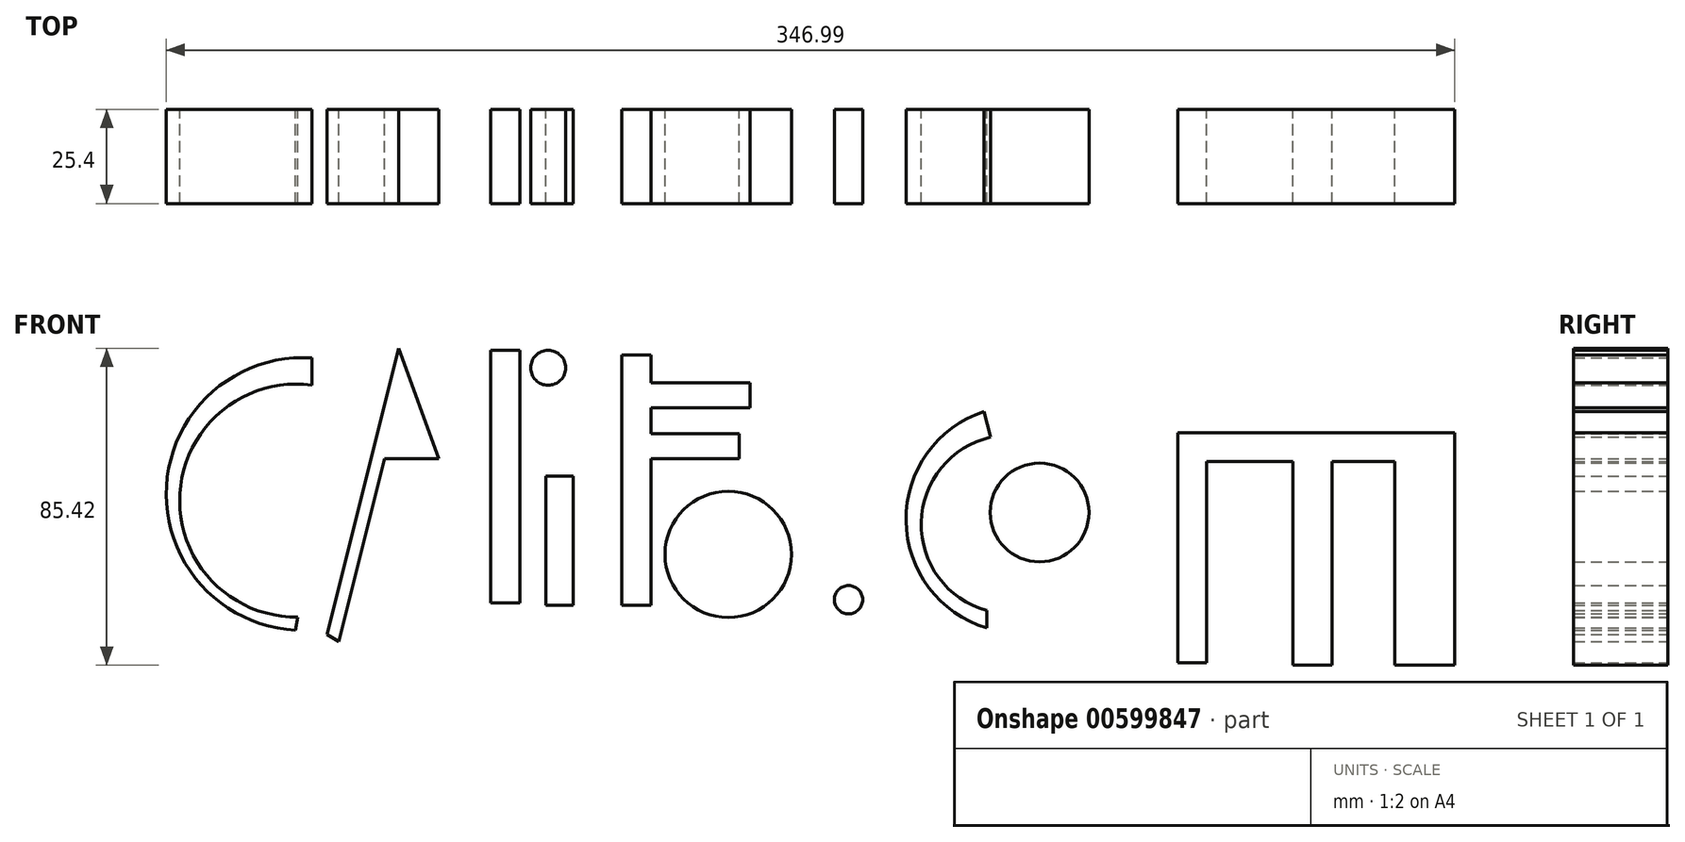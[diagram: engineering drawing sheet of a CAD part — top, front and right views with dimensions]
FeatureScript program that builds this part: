
annotation { "Feature Type Name" : "Feature", "Feature Type Description" : "" }
export const myFeature = defineFeature(function(context is Context, id is Id, definition is map)
    precondition{}
    {
        {
            var Q0;
            Q0=qCreatedBy(makeId("Front.planeOp"),FACE);
            var sketch = newSketch(context, id + "F0", { "sketchPlane" : qUnion([Q0])});
            skArc(sketch, "E0", {"start": v(-27.89, 41.61) * mm, "mid": v(-67, 7.17) * mm, "end": v(-32.27, -31.68) * mm});
            skLineSegment(sketch, "E1", {"start": v(-4.53, 44.24) * mm, "end": v(-23.8, -32.85) * mm});
            skLineSegment(sketch, "E2", {"start": v(-4.53, 44.24) * mm, "end": v(20.3, -24.38) * mm});
            skLineSegment(sketch, "E3", {"start": v(6.25, 14.44) * mm, "end": v(-11.97, 14.44) * mm});
            skLineSegment(sketch, "E4", {"start": v(28.12, 43.68) * mm, "end": v(28.12, -24.97) * mm});
            skLineSegment(sketch, "E5", {"start": v(35.19, 19.13) * mm, "end": v(35.19, -24.38) * mm});
            skCircle(sketch, "E6", {"center": v(35.77, 38.98) * mm, "radius": 4.7 * mm});
            skLineSegment(sketch, "E7", {"start": v(55.63, 42.49) * mm, "end": v(55.63, -22.63) * mm});
            skLineSegment(sketch, "E8", {"start": v(55.63, -22.63) * mm, "end": v(55.63, 34.9) * mm});
            skLineSegment(sketch, "E9", {"start": v(55.63, 34.9) * mm, "end": v(75.78, 34.9) * mm});
            skLineSegment(sketch, "E10", {"start": v(55.63, 21.17) * mm, "end": v(77.24, 21.17) * mm});
            skLineSegment(sketch, "E11.bottom", {"start": v(35.19, 9.78) * mm, "end": v(42.49, 9.78) * mm});
            skLineSegment(sketch, "E11.top", {"start": v(35.19, -24.97) * mm, "end": v(42.49, -24.97) * mm});
            skLineSegment(sketch, "E11.left", {"start": v(35.19, 9.78) * mm, "end": v(35.19, -24.97) * mm});
            skLineSegment(sketch, "E11.right", {"start": v(42.49, 9.78) * mm, "end": v(42.49, -24.97) * mm});
            skLineSegment(sketch, "E12.bottom", {"start": v(55.63, 34.9) * mm, "end": v(55.63, 34.9) * mm});
            skLineSegment(sketch, "E12.top", {"start": v(55.63, 42.49) * mm, "end": v(55.63, 42.49) * mm});
            skLineSegment(sketch, "E12.left", {"start": v(55.63, 34.9) * mm, "end": v(55.63, 42.49) * mm});
            skLineSegment(sketch, "E12.right", {"start": v(55.63, 34.9) * mm, "end": v(55.63, 42.49) * mm});
            skLineSegment(sketch, "E13.bottom", {"start": v(55.63, 42.49) * mm, "end": v(63.51, 42.49) * mm});
            skLineSegment(sketch, "E13.top", {"start": v(55.63, -24.97) * mm, "end": v(63.51, -24.97) * mm});
            skLineSegment(sketch, "E13.left", {"start": v(55.63, 42.49) * mm, "end": v(55.63, -24.97) * mm});
            skLineSegment(sketch, "E13.right", {"start": v(63.51, 42.49) * mm, "end": v(63.51, -24.97) * mm});
            skLineSegment(sketch, "E14.bottom", {"start": v(55.63, 34.9) * mm, "end": v(90.08, 34.9) * mm});
            skLineSegment(sketch, "E14.top", {"start": v(55.63, 28.18) * mm, "end": v(90.08, 28.18) * mm});
            skLineSegment(sketch, "E14.left", {"start": v(55.63, 34.9) * mm, "end": v(55.63, 28.18) * mm});
            skLineSegment(sketch, "E14.right", {"start": v(90.08, 34.9) * mm, "end": v(90.08, 28.18) * mm});
            skLineSegment(sketch, "E15.bottom", {"start": v(55.63, 14.44) * mm, "end": v(87.16, 14.44) * mm});
            skLineSegment(sketch, "E15.top", {"start": v(55.63, 21.17) * mm, "end": v(87.16, 21.17) * mm});
            skLineSegment(sketch, "E15.left", {"start": v(55.63, 14.44) * mm, "end": v(55.63, 21.17) * mm});
            skLineSegment(sketch, "E15.right", {"start": v(87.16, 14.44) * mm, "end": v(87.16, 21.17) * mm});
            skArc(sketch, "E16", {"start": v(-27.89, 34.31) * mm, "mid": v(-63.41, 5.1) * mm, "end": v(-31.68, -28.18) * mm});
            skLineSegment(sketch, "E17", {"start": v(-27.89, 41.61) * mm, "end": v(-27.89, 34.31) * mm});
            skLineSegment(sketch, "E18", {"start": v(-31.68, -28.18) * mm, "end": v(-32.27, -31.68) * mm});
            skLineSegment(sketch, "E19", {"start": v(-8.32, 14.44) * mm, "end": v(-20.62, -34.74) * mm});
            skLineSegment(sketch, "E20", {"start": v(-20.62, -34.74) * mm, "end": v(-23.8, -32.85) * mm});
            skLineSegment(sketch, "E21", {"start": v(0, 14.44) * mm, "end": v(14.04, -24.38) * mm});
            skLineSegment(sketch, "E22.bottom", {"start": v(28.12, 43.68) * mm, "end": v(20.3, 43.68) * mm});
            skLineSegment(sketch, "E22.top", {"start": v(28.12, -24.38) * mm, "end": v(20.3, -24.38) * mm});
            skLineSegment(sketch, "E22.left", {"start": v(28.12, 43.68) * mm, "end": v(28.12, -24.38) * mm});
            skLineSegment(sketch, "E22.right", {"start": v(20.3, 43.68) * mm, "end": v(20.3, -24.38) * mm});
            skCircle(sketch, "E23", {"center": v(84.26, -11.3) * mm, "radius": 17.02 * mm});
            skLineSegment(sketch, "E24", {"start": v(106.25, -25.76) * mm, "end": v(106.25, 8.96) * mm});
            skLineSegment(sketch, "E25", {"start": v(106.25, 0) * mm, "end": v(125.95, 4.73) * mm});
            skSolve(sketch);
        }
        {
            var Q0;
            Q0 = qSketchRegion(id + "F0", true);
            extrude(context, id + "F1", {"entities" : qUnion([Q0]), "depth" : 25.4 * mm, "offsetDistance" : 25.4 * mm});
        }
        {
            var Q0;
            Q0=qCreatedBy(makeId("Front.planeOp"),FACE);
            var sketch = newSketch(context, id + "F2", { "sketchPlane" : qUnion([Q0])});
            skCircle(sketch, "E26", {"center": v(116.64, -23.5) * mm, "radius": 3.8 * mm});
            skArc(sketch, "E27", {"start": v(153.14, 27.23) * mm, "mid": v(132.12, -2.23) * mm, "end": v(153.87, -31.16) * mm});
            skArc(sketch, "E28", {"start": v(154.96, 20.3) * mm, "mid": v(136.21, -2.63) * mm, "end": v(153.87, -26.41) * mm});
            skLineSegment(sketch, "E29", {"start": v(153.14, 27.23) * mm, "end": v(154.96, 20.3) * mm});
            skLineSegment(sketch, "E30", {"start": v(153.87, -26.41) * mm, "end": v(153.87, -31.16) * mm});
            skCircle(sketch, "E31", {"center": v(168.1, 0) * mm, "radius": 13.3 * mm});
            skLineSegment(sketch, "E32.bottom", {"start": v(205.3, 21.47) * mm, "end": v(213.04, 21.47) * mm});
            skLineSegment(sketch, "E32.top", {"start": v(205.3, -40.48) * mm, "end": v(213.04, -40.48) * mm});
            skLineSegment(sketch, "E32.left", {"start": v(205.3, 21.47) * mm, "end": v(205.3, -40.48) * mm});
            skLineSegment(sketch, "E32.right", {"start": v(213.04, 21.47) * mm, "end": v(213.04, -40.48) * mm});
            skLineSegment(sketch, "E33.bottom", {"start": v(213.04, 21.47) * mm, "end": v(236.27, 21.47) * mm});
            skLineSegment(sketch, "E33.top", {"start": v(213.04, 13.72) * mm, "end": v(236.27, 13.72) * mm});
            skLineSegment(sketch, "E33.left", {"start": v(213.04, 21.47) * mm, "end": v(213.04, 13.72) * mm});
            skLineSegment(sketch, "E33.right", {"start": v(236.27, 21.47) * mm, "end": v(236.27, 13.72) * mm});
            skLineSegment(sketch, "E34.bottom", {"start": v(236.27, 21.47) * mm, "end": v(246.83, 21.47) * mm});
            skLineSegment(sketch, "E34.top", {"start": v(236.27, -41.18) * mm, "end": v(246.83, -41.18) * mm});
            skLineSegment(sketch, "E34.left", {"start": v(236.27, 21.47) * mm, "end": v(236.27, -41.18) * mm});
            skLineSegment(sketch, "E34.right", {"start": v(246.83, 21.47) * mm, "end": v(246.83, -41.18) * mm});
            skLineSegment(sketch, "E35.bottom", {"start": v(246.83, 21.47) * mm, "end": v(279.92, 21.47) * mm});
            skLineSegment(sketch, "E35.top", {"start": v(246.83, 13.72) * mm, "end": v(279.92, 13.72) * mm});
            skLineSegment(sketch, "E35.left", {"start": v(246.83, 21.47) * mm, "end": v(246.83, 13.72) * mm});
            skLineSegment(sketch, "E35.right", {"start": v(279.92, 21.47) * mm, "end": v(279.92, 13.72) * mm});
            skLineSegment(sketch, "E36.bottom", {"start": v(279.92, 21.47) * mm, "end": v(279.92, 21.47) * mm});
            skLineSegment(sketch, "E36.top", {"start": v(279.92, -41.18) * mm, "end": v(279.92, -41.18) * mm});
            skLineSegment(sketch, "E36.left", {"start": v(279.92, 21.47) * mm, "end": v(279.92, -41.18) * mm});
            skLineSegment(sketch, "E36.right", {"start": v(279.92, 21.47) * mm, "end": v(279.92, -41.18) * mm});
            skLineSegment(sketch, "E37.bottom", {"start": v(279.92, -41.18) * mm, "end": v(263.72, -41.18) * mm});
            skLineSegment(sketch, "E37.top", {"start": v(279.92, -41.18) * mm, "end": v(263.72, -41.18) * mm});
            skLineSegment(sketch, "E37.right", {"start": v(263.72, -41.18) * mm, "end": v(263.72, -41.18) * mm});
            skLineSegment(sketch, "E38", {"start": v(263.72, -41.18) * mm, "end": v(263.72, 13.72) * mm});
            skSolve(sketch);
        }
        {
            var Q0;
            Q0 = qSketchRegion(id + "F2", true);
            extrude(context, id + "F3", {"entities" : qUnion([Q0]), "depth" : 25.4 * mm, "offsetDistance" : 25.4 * mm});
        }
    });
